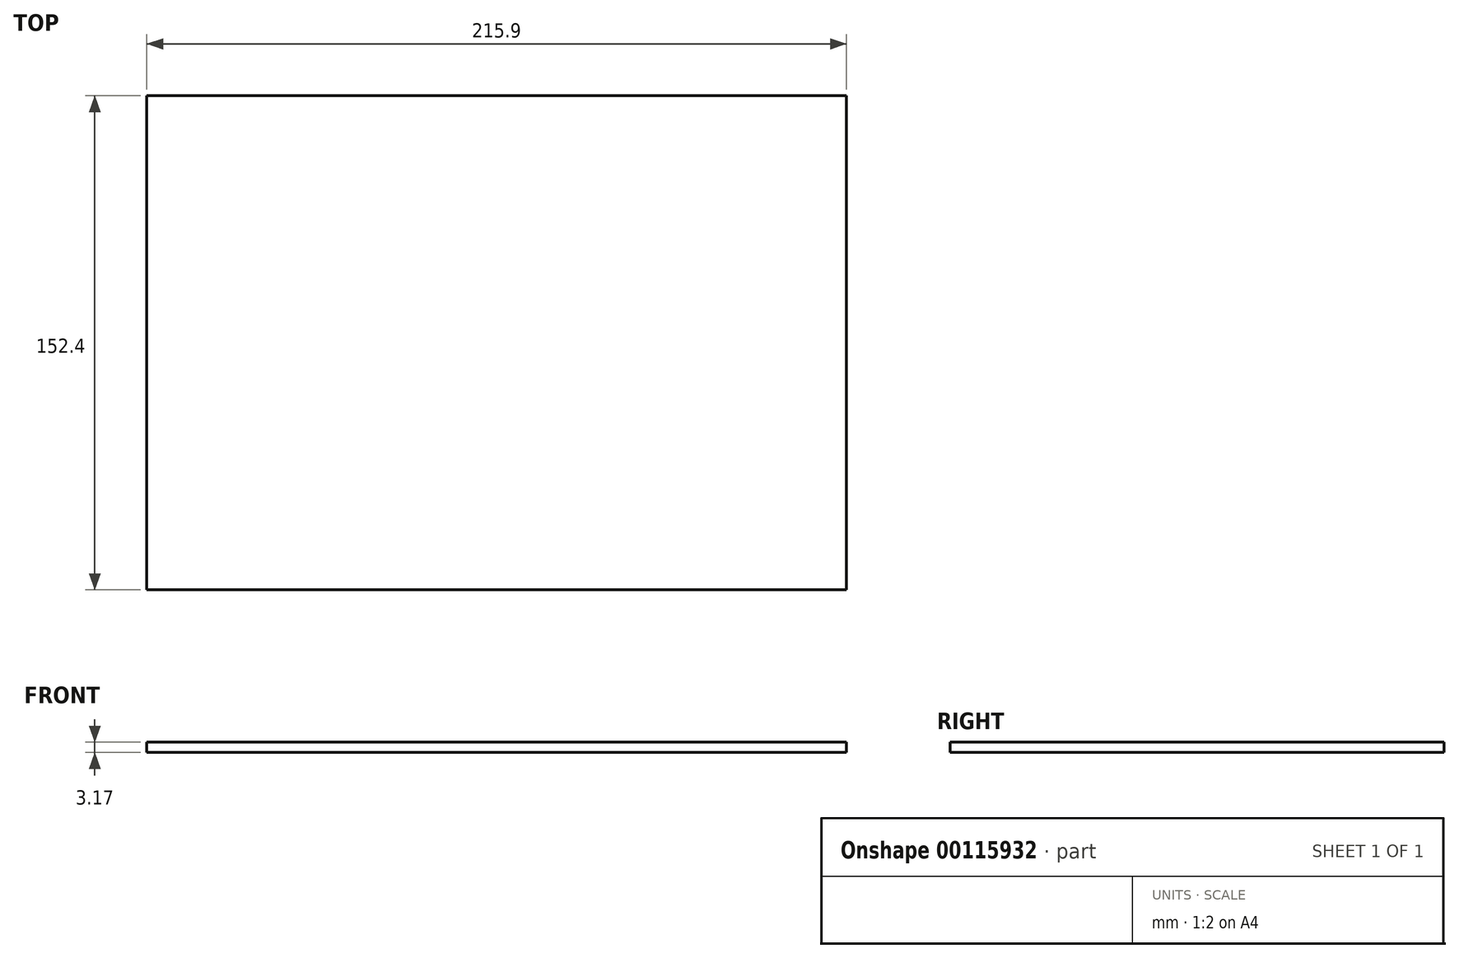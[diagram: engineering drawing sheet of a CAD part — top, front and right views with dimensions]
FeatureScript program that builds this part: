
annotation { "Feature Type Name" : "Feature", "Feature Type Description" : "" }
export const myFeature = defineFeature(function(context is Context, id is Id, definition is map)
    precondition{}
    {
        {
            var Q0;
            Q0=qCreatedBy(makeId("Top.planeOp"),FACE);
            var sketch = newSketch(context, id + "F0", { "sketchPlane" : qUnion([Q0])});
            skLineSegment(sketch, "E0.bottom", {"start": v(-117.04, 49.95) * mm, "end": v(98.86, 49.95) * mm});
            skLineSegment(sketch, "E0.top", {"start": v(-117.04, -102.45) * mm, "end": v(98.86, -102.45) * mm});
            skLineSegment(sketch, "E0.left", {"start": v(-117.04, 49.95) * mm, "end": v(-117.04, -102.45) * mm});
            skLineSegment(sketch, "E0.right", {"start": v(98.86, 49.95) * mm, "end": v(98.86, -102.45) * mm});
            skSolve(sketch);
        }
        {
            var Q0;
            Q0=makeQuery(id+"F0.imprint","IMPRINT",FACE,{"disambiguationData":[TD([[makeQuery(id+"F0.imprint","IMPRINT",EDGE,{"derivedFrom":sQuery(id+"F0.wireOp",EDGE,"E0.bottom")}),-1.0]])]});
            extrude(context, id + "F1", {"entities" : qUnion([Q0]), "depth" : 3.17 * mm});
        }
    });
